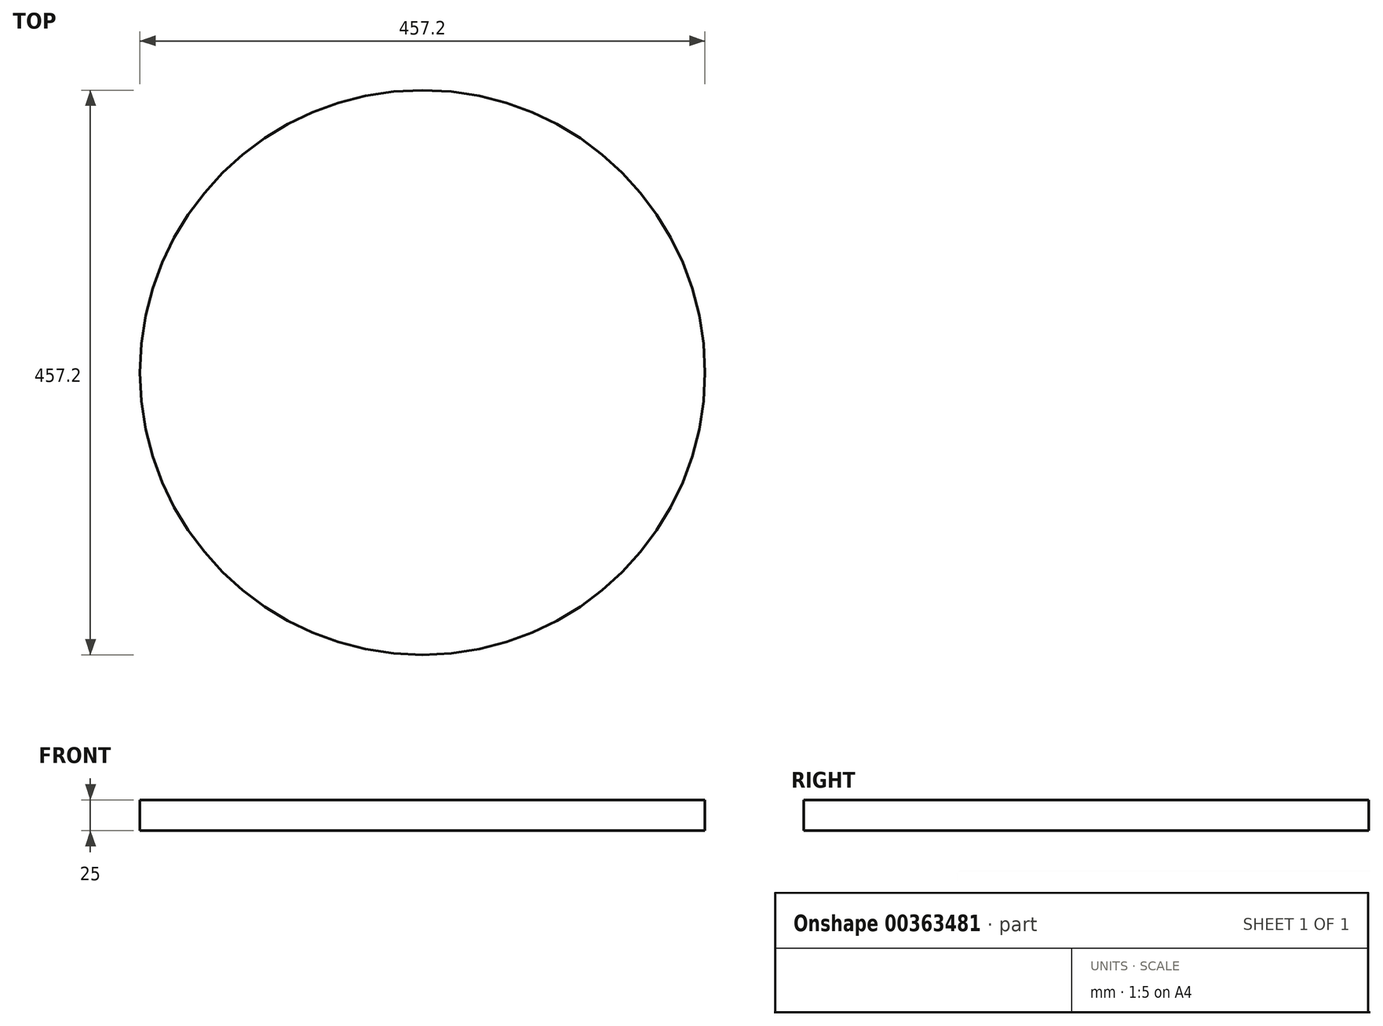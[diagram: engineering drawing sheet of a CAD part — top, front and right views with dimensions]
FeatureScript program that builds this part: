
annotation { "Feature Type Name" : "Feature", "Feature Type Description" : "" }
export const myFeature = defineFeature(function(context is Context, id is Id, definition is map)
    precondition{}
    {
        {
            var Q0;
            Q0=qCreatedBy(makeId("Top.planeOp"),FACE);
            var sketch = newSketch(context, id + "F0", { "sketchPlane" : qUnion([Q0])});
            skCircle(sketch, "E0", {"center": v(0, 0) * mm, "radius": 228.6 * mm});
            skSolve(sketch);
        }
        {
            var Q0;
            Q0=makeQuery(id+"F0.imprint","IMPRINT",FACE,{"disambiguationData":[TD([[makeQuery(id+"F0.imprint","IMPRINT",EDGE,{"derivedFrom":sQuery(id+"F0.wireOp",EDGE,"E0")}),1.0]])]});
            extrude(context, id + "F1", {"entities" : qUnion([Q0]), "depth" : 25 * mm});
        }
    });
